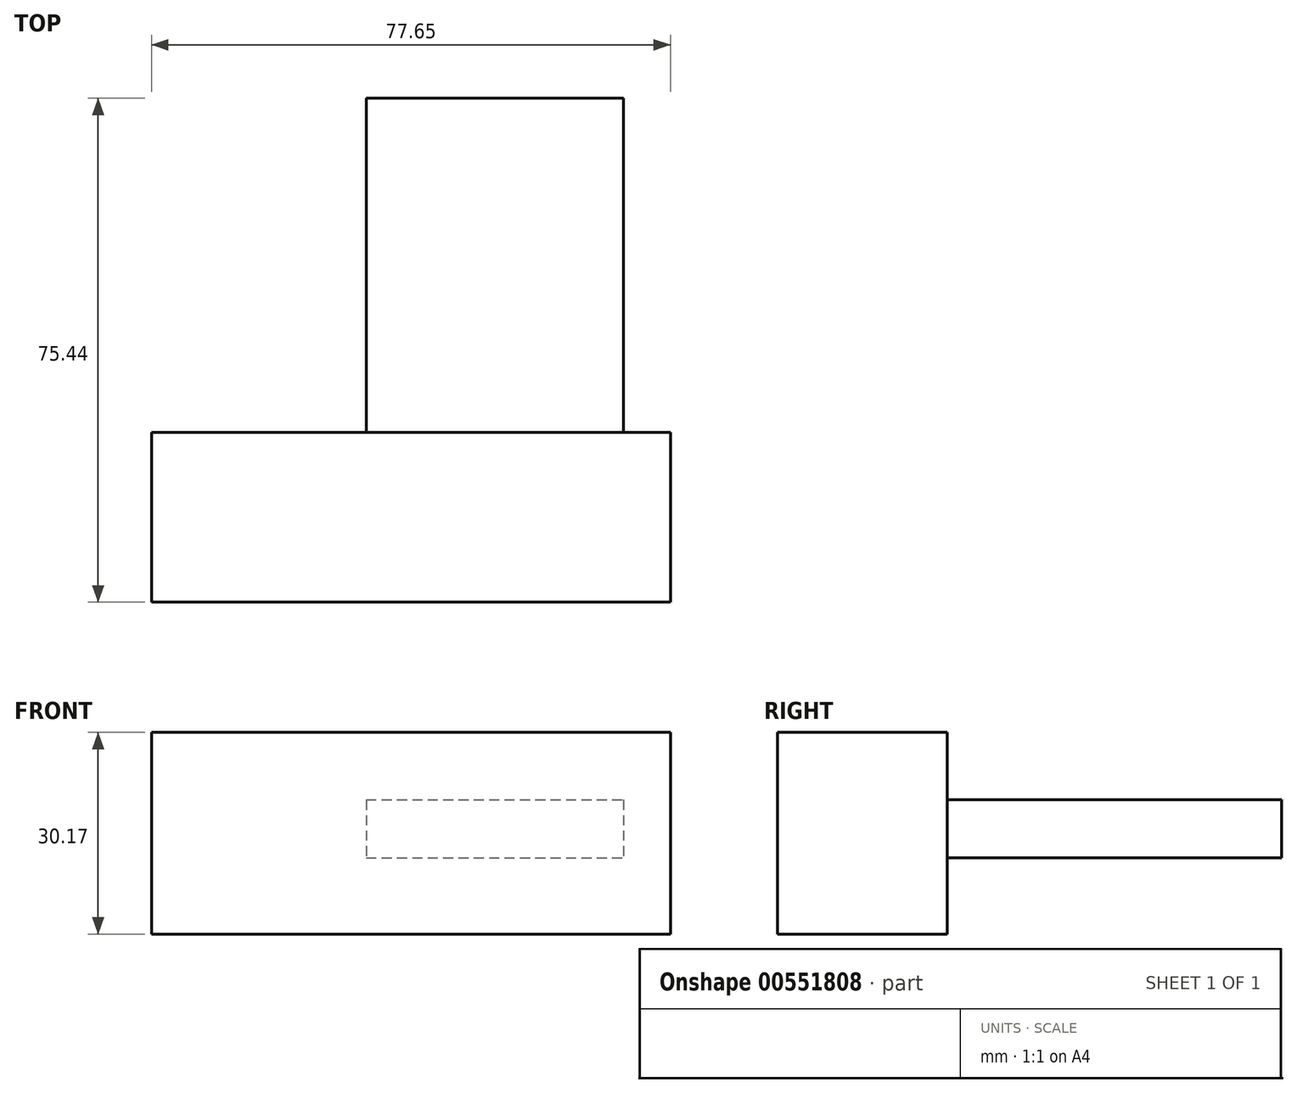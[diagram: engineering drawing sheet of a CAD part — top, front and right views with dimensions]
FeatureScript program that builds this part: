
annotation { "Feature Type Name" : "Feature", "Feature Type Description" : "" }
export const myFeature = defineFeature(function(context is Context, id is Id, definition is map)
    precondition{}
    {
        {
            var Q0;
            Q0=qCreatedBy(makeId("Front.planeOp"),FACE);
            var sketch = newSketch(context, id + "F0", { "sketchPlane" : qUnion([Q0])});
            skLineSegment(sketch, "E0.bottom", {"start": v(-49.02, 30.17) * mm, "end": v(28.63, 30.17) * mm});
            skLineSegment(sketch, "E0.top", {"start": v(-49.02, 0) * mm, "end": v(28.63, 0) * mm});
            skLineSegment(sketch, "E0.left", {"start": v(-49.02, 30.17) * mm, "end": v(-49.02, 0) * mm});
            skLineSegment(sketch, "E0.right", {"start": v(28.63, 30.17) * mm, "end": v(28.63, 0) * mm});
            skSolve(sketch);
        }
        {
            var Q0;
            Q0 = qSketchRegion(id + "F0", true);
            extrude(context, id + "F1", {"entities" : qUnion([Q0]), "depth" : 25.4 * mm, "offsetDistance" : 25.4 * mm});
        }
        {
            var Q0;
            Q0=qCreatedBy(makeId("Front.planeOp"),FACE);
            var sketch = newSketch(context, id + "F2", { "sketchPlane" : qUnion([Q0])});
            skLineSegment(sketch, "E1.bottom", {"start": v(-16.89, 20.08) * mm, "end": v(21.62, 20.08) * mm});
            skLineSegment(sketch, "E1.top", {"start": v(-16.89, 11.43) * mm, "end": v(21.62, 11.43) * mm});
            skLineSegment(sketch, "E1.left", {"start": v(-16.89, 20.08) * mm, "end": v(-16.89, 11.43) * mm});
            skLineSegment(sketch, "E1.right", {"start": v(21.62, 20.08) * mm, "end": v(21.62, 11.43) * mm});
            skSolve(sketch);
        }
        {
            var Q0;
            Q0 = qSketchRegion(id + "F2", true);
            extrude(context, id + "F3", {"entities" : qUnion([Q0]), "operationType" : NewBodyOperationType.ADD, "oppositeDirection" : true, "depth" : 50.04 * mm, "offsetDistance" : 25.4 * mm});
        }
    });
